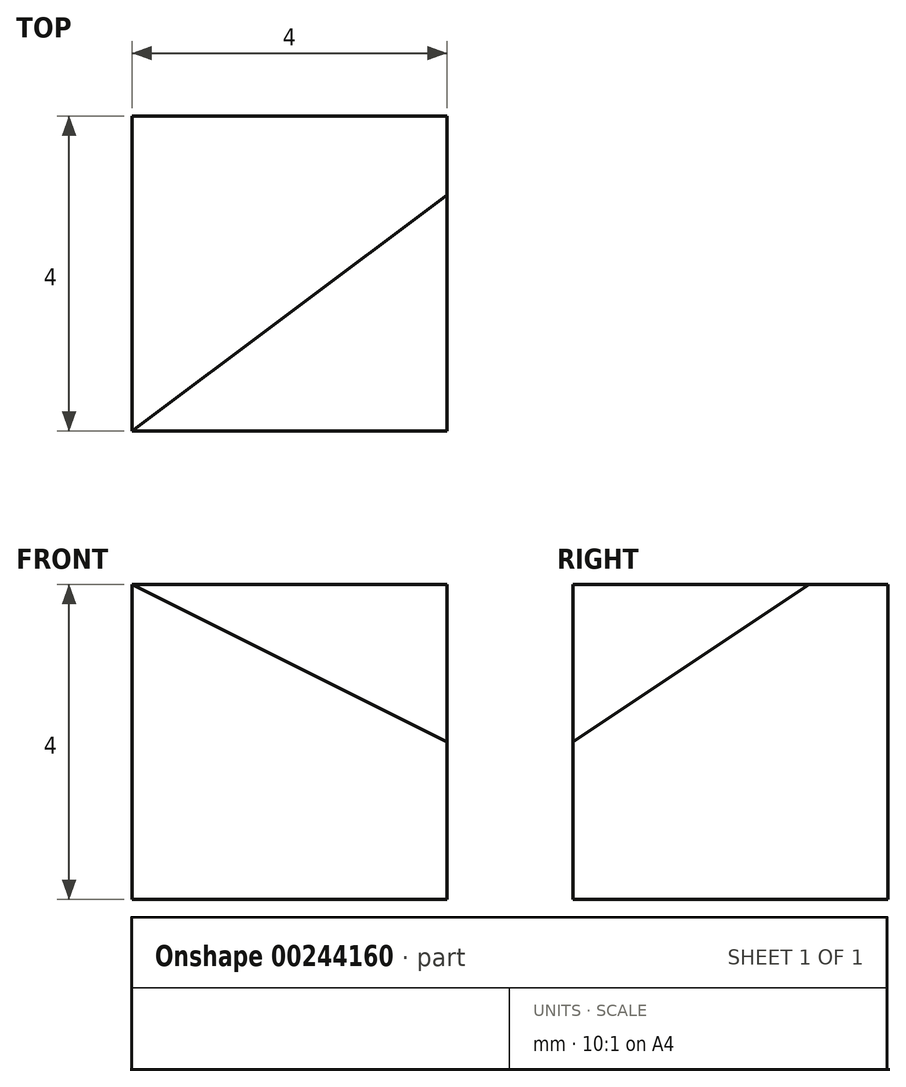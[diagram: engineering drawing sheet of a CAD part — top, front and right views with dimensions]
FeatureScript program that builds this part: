
annotation { "Feature Type Name" : "Feature", "Feature Type Description" : "" }
export const myFeature = defineFeature(function(context is Context, id is Id, definition is map)
    precondition{}
    {
        {
            var Q0;
            Q0=qCreatedBy(makeId("Top.planeOp"),FACE);
            var sketch = newSketch(context, id + "F0", { "sketchPlane" : qUnion([Q0])});
            skLineSegment(sketch, "E0.bottom", {"start": v(0, 0) * mm, "end": v(4, 0) * mm});
            skLineSegment(sketch, "E0.top", {"start": v(0, 4) * mm, "end": v(4, 4) * mm});
            skLineSegment(sketch, "E0.left", {"start": v(0, 0) * mm, "end": v(0, 4) * mm});
            skLineSegment(sketch, "E0.right", {"start": v(4, 0) * mm, "end": v(4, 4) * mm});
            skSolve(sketch);
        }
        {
            var Q0;
            Q0 = qSketchRegion(id + "F0", true);
            extrude(context, id + "F1", {"entities" : qUnion([Q0]), "depth" : 4 * mm});
        }
        {
            var Q0;
            Q0=makeQuery(id+"F1.opExtrude","SWEPT_FACE",FACE,{"disambiguationData":[OSD([sQuery(id+"F0.wireOp",EDGE,"E0.bottom")])]});
            var sketch = newSketch(context, id + "F2", { "sketchPlane" : qUnion([Q0])});
            skLineSegment(sketch, "E1", {"start": v(4, 0) * mm, "end": v(4, 2) * mm, "construction": true});
            skSolve(sketch);
        }
        {
            var Q0;
            Q0=makeQuery(id+"F1.opExtrude","SWEPT_FACE",FACE,{"disambiguationData":[OSD([sQuery(id+"F0.wireOp",EDGE,"E0.right")])]});
            var sketch = newSketch(context, id + "F3", { "sketchPlane" : qUnion([Q0])});
            skLineSegment(sketch, "E2", {"start": v(4, 4) * mm, "end": v(3, 4) * mm, "construction": true});
            skSolve(sketch);
        }
        {
            var Q0;
            Q0=makeQuery(id+"F1.opExtrude","CAP_VERTEX",VERTEX,{"disambiguationData":[OSD([sQuery(id+"F0.wireOp",EDGE,"E0.bottom"),sQuery(id+"F0.wireOp",EDGE,"E0.left")])],"isStart":false});
            var Q1;
            Q1=sQuery(id+"F3.wireOp",VERTEX,"E2.end");
            var Q2;
            Q2=sQuery(id+"F2.wireOp",VERTEX,"E1.end");
            cPlane(context, id + "F4", {"entities" : qUnion([Q0, Q1, Q2]), "cplaneType" : CPlaneType.THREE_POINT, "offset" : 25 * mm, "width" : 150 * mm, "height" : 150 * mm});
        }
        {
            var Q0;
            Q0=qCreatedBy(id+"F4.planeOp",FACE);
            var sketch = newSketch(context, id + "F5", { "sketchPlane" : qUnion([Q0])});
            skPoint(sketch, "E3.0", {"position": v(-1.28, 2.22) * mm});
            skPoint(sketch, "E3.1", {"position": v(3.05, 4.71) * mm});
            skPoint(sketch, "E3.2", {"position": v(3.05, 1.1) * mm});
            skLineSegment(sketch, "E4", {"start": v(-1.28, 2.22) * mm, "end": v(3.05, 4.71) * mm});
            skLineSegment(sketch, "E5", {"start": v(3.05, 1.1) * mm, "end": v(3.05, 4.71) * mm});
            skLineSegment(sketch, "E6", {"start": v(3.05, 1.1) * mm, "end": v(-1.28, 2.22) * mm});
            skSolve(sketch);
        }
        {
            var Q0;
            Q0 = qSketchRegion(id + "F5", true);
            extrude(context, id + "F6", {"entities" : qUnion([Q0]), "operationType" : NewBodyOperationType.REMOVE, "depth" : 25 * mm});
        }
    });
